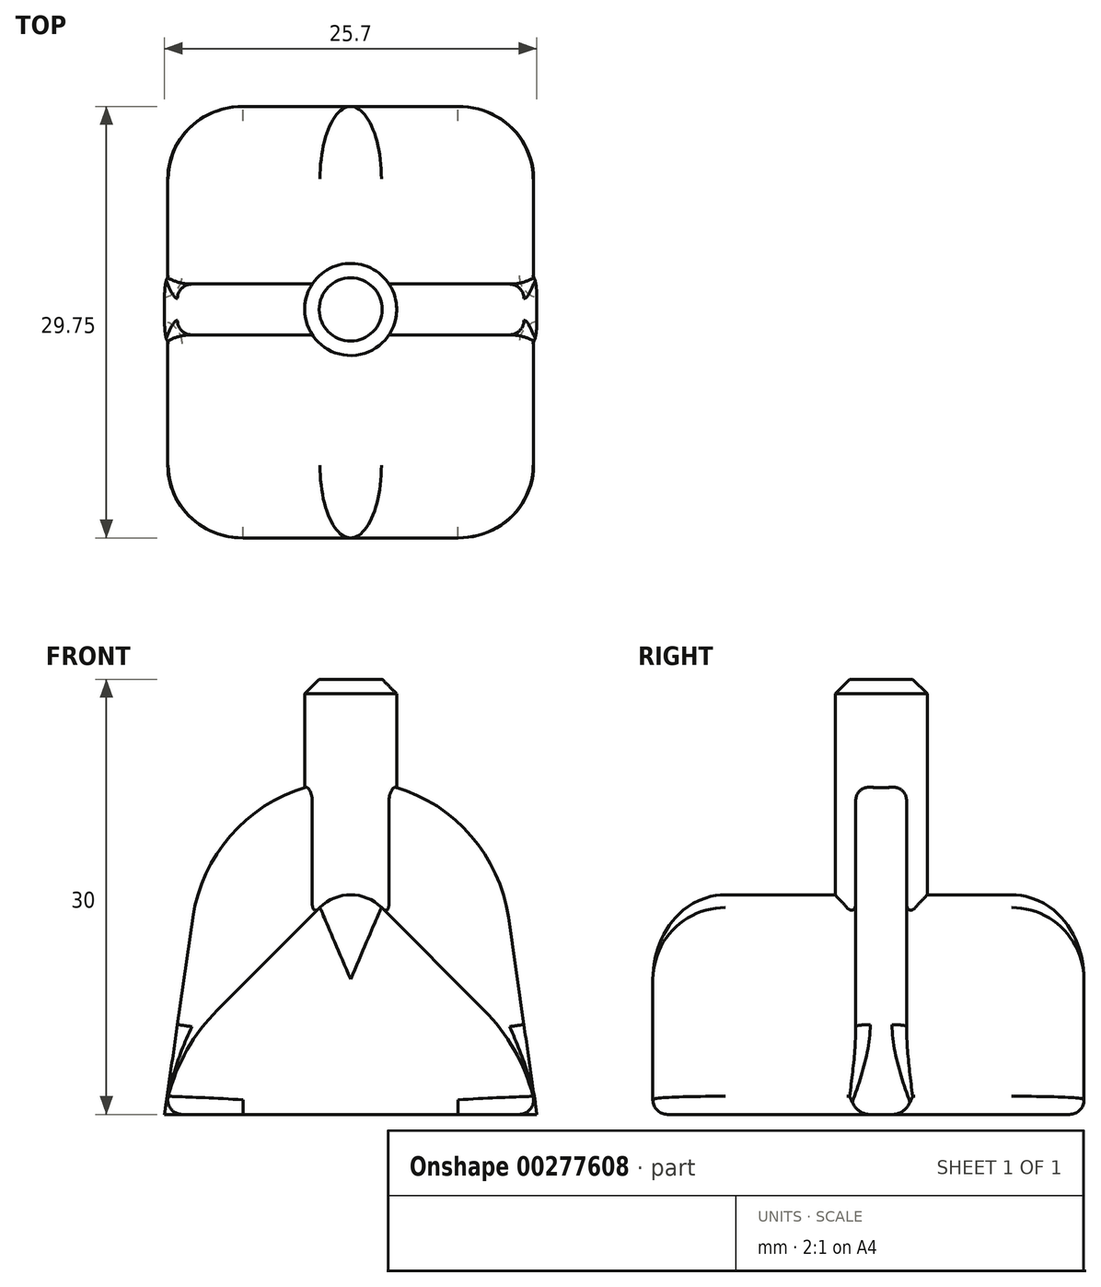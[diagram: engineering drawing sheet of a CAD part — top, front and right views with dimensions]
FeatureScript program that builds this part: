
annotation { "Feature Type Name" : "Feature", "Feature Type Description" : "" }
export const myFeature = defineFeature(function(context is Context, id is Id, definition is map)
    precondition{}
    {
        {
            var Q0;
            Q0=qCreatedBy(makeId("Front.planeOp"),FACE);
            var sketch = newSketch(context, id + "F0", { "sketchPlane" : qUnion([Q0])});
            skArc(sketch, "E0", {"start": v(12.85, 0) * mm, "mid": v(0, 11) * mm, "end": v(-12.85, 0) * mm});
            skLineSegment(sketch, "E1", {"start": v(-9.2, 7.2) * mm, "end": v(-2.12, 14.26) * mm});
            skLineSegment(sketch, "E2", {"start": v(2.12, 14.26) * mm, "end": v(9.2, 7.2) * mm});
            skLineSegment(sketch, "E3", {"start": v(12.85, 0) * mm, "end": v(-12.85, 0) * mm});
            skPoint(sketch, "E4.visualSharp", {"position": v(0, 16.38) * mm});
            skArc(sketch, "E4.filletArc", {"start": v(2.12, 14.26) * mm, "mid": v(0, 15.14) * mm, "end": v(-2.12, 14.26) * mm});
            skCircle(sketch, "E5", {"center": v(0, 12) * mm, "radius": 11 * mm, "construction": true});
            skSolve(sketch);
        }
        {
            var Q0;
            {var subQ0=sQuery(id+"F0.wireOp",EDGE,"E3");Q0=makeQuery(id+"F0.imprint","IMPRINT",FACE,{"disambiguationData":[TD([[makeQuery(id+"F0.imprint","IMPRINT",EDGE,{"derivedFrom":subQ0}),-1.0]])]});}
            var Q1;
            {var subQ0=sQuery(id+"F0.wireOp",EDGE,"E1");Q1=makeQuery(id+"F0.imprint","IMPRINT",FACE,{"disambiguationData":[TD([[makeQuery(id+"F0.imprint","IMPRINT",EDGE,{"derivedFrom":subQ0}),-1.0]])]});}
            extrude(context, id + "F1", {"entities" : qUnion([Q0, Q1]), "endBound" : BoundingType.SYMMETRIC, "depth" : 28 * mm});
        }
        {
            var Q0;
            Q0=qCreatedBy(makeId("Front.planeOp"),FACE);
            var sketch = newSketch(context, id + "F2", { "sketchPlane" : qUnion([Q0])});
            skCircle(sketch, "E6.0", {"center": v(0, 12) * mm, "radius": 11 * mm});
            skArc(sketch, "E7.0", {"start": v(12.85, 0) * mm, "mid": v(0, 11) * mm, "end": v(-12.85, 0) * mm});
            skLineSegment(sketch, "E8", {"start": v(-10.89, 13.57) * mm, "end": v(-12.85, 0) * mm});
            skLineSegment(sketch, "E9", {"start": v(10.89, 13.57) * mm, "end": v(12.85, 0) * mm});
            skLineSegment(sketch, "E10.0", {"start": v(12.85, 0) * mm, "end": v(-12.85, 0) * mm});
            skSolve(sketch);
        }
        {
            var Q0;
            {var subQ0=sQuery(id+"F2.wireOp",EDGE,"E6.0");var subQ1=makeQuery(id+"F2.imprint","INTERSECT",VERTEX,{"derivedFrom":[subQ0,sQuery(id+"F2.wireOp",EDGE,"E8")]});Q0=makeQuery(id+"F2.imprint","IMPRINT",FACE,{"disambiguationData":[TD([[makeQuery(id+"F2.imprint","IMPRINT",EDGE,{"disambiguationData":[TD([[subQ1,1.0]])],"derivedFrom":subQ0}),1.0]])]});}
            var Q1;
            {var subQ0=sQuery(id+"F2.wireOp",EDGE,"E8");Q1=makeQuery(id+"F2.imprint","IMPRINT",FACE,{"disambiguationData":[TD([[makeQuery(id+"F2.imprint","IMPRINT",EDGE,{"derivedFrom":subQ0}),1.0]])]});}
            var Q2;
            Q2=makeQuery(id+"F1.opExtrude","CAP_FACE",FACE,{"disambiguationData":[OSD([sQuery(id+"F0.wireOp",EDGE,"E0"),sQuery(id+"F0.wireOp",EDGE,"E1"),sQuery(id+"F0.wireOp",EDGE,"E2"),sQuery(id+"F0.wireOp",EDGE,"E3"),sQuery(id+"F0.wireOp",EDGE,"E4.filletArc")])],"isStart":false});
            var Q3;
            {var subQ0=sQuery(id+"F2.wireOp",EDGE,"E9");Q3=makeQuery(id+"F2.imprint","IMPRINT",FACE,{"disambiguationData":[TD([[makeQuery(id+"F2.imprint","IMPRINT",EDGE,{"derivedFrom":subQ0}),-1.0]])]});}
            extrude(context, id + "F3", {"entities" : qUnion([Q0, Q1, Q2, Q3]), "operationType" : NewBodyOperationType.ADD, "endBound" : BoundingType.SYMMETRIC, "depth" : 3.5 * mm});
        }
        {
            var Q0;
            {var subQ0=sQuery(id+"F0.wireOp",EDGE,"E0");Q0=makeQuery(id+"F3.opExtrude","CAP_EDGE",EDGE,{"disambiguationData":[OSD([subQ0]),TDD([makeQuery(id+"F1.opExtrude","CAP_EDGE",EDGE,{"disambiguationData":[OSD([subQ0]),TDD([makeQuery(id+"F0.imprint","IMPRINT",EDGE,{"disambiguationData":[TD([[makeQuery(id+"F0.imprint","INTERSECT",VERTEX,{"disambiguationData":[OD(0.0)],"derivedFrom":[subQ0,sQuery(id+"F0.wireOp",EDGE,"E3")]}),-1.0]])],"derivedFrom":subQ0})])],"isStart":false})])],"isStart":false});}
            var Q1;
            {var subQ0=sQuery(id+"F0.wireOp",EDGE,"E0");Q1=makeQuery(id+"F1.opExtrude","CAP_EDGE",EDGE,{"disambiguationData":[OSD([subQ0]),TDD([makeQuery(id+"F0.imprint","IMPRINT",EDGE,{"disambiguationData":[TD([[makeQuery(id+"F0.imprint","INTERSECT",VERTEX,{"disambiguationData":[OD(0.0)],"derivedFrom":[subQ0,sQuery(id+"F0.wireOp",EDGE,"E3")]}),-1.0]])],"derivedFrom":subQ0})])],"isStart":true});}
            fillet(context, id + "F4", {"entities" : qUnion([Q0, Q1]), "radius" : 5 * mm, "tangentPropagation" : true, "allowEdgeOverflow" : false});
        }
        {
            var Q0;
            {var subQ0=sQuery(id+"F0.wireOp",EDGE,"E0");var subQ1=makeQuery(id+"F0.imprint","IMPRINT",EDGE,{"disambiguationData":[TD([[makeQuery(id+"F0.imprint","INTERSECT",VERTEX,{"disambiguationData":[OD(1.0)],"derivedFrom":[subQ0,sQuery(id+"F0.wireOp",EDGE,"E3")]}),1.0]])],"derivedFrom":subQ0});var subQ2=sQuery(id+"F2.wireOp",EDGE,"E7.0");Q0=makeQuery(id+"F3.boolean.opBoolean","SPLIT",EDGE,{"disambiguationData":[topologyDisambiguationEdgeConnected([makeQuery(id+"F3.opExtrude","SWEPT_FACE",FACE,{"disambiguationData":[OSD([subQ0]),TDD([makeQuery(id+"F1.opExtrude","CAP_EDGE",EDGE,{"disambiguationData":[OSD([subQ0]),TDD([subQ1])],"isStart":false})])]})])],"derivedFrom":makeQuery(id+"F3.opExtrude","CAP_EDGE",EDGE,{"disambiguationData":[OSD([subQ2])],"isStart":false})});}
            var Q1;
            {var subQ0=sQuery(id+"F0.wireOp",EDGE,"E0");var subQ1=makeQuery(id+"F0.imprint","IMPRINT",EDGE,{"disambiguationData":[TD([[makeQuery(id+"F0.imprint","INTERSECT",VERTEX,{"disambiguationData":[OD(1.0)],"derivedFrom":[subQ0,sQuery(id+"F0.wireOp",EDGE,"E3")]}),1.0]])],"derivedFrom":subQ0});var subQ2=sQuery(id+"F2.wireOp",EDGE,"E7.0");Q1=makeQuery(id+"F3.boolean.opBoolean","SPLIT",EDGE,{"disambiguationData":[topologyDisambiguationEdgeConnected([makeQuery(id+"F3.opExtrude","SWEPT_FACE",FACE,{"disambiguationData":[OSD([subQ0]),TDD([makeQuery(id+"F1.opExtrude","CAP_EDGE",EDGE,{"disambiguationData":[OSD([subQ0]),TDD([subQ1])],"isStart":false})])]})])],"derivedFrom":makeQuery(id+"F3.opExtrude","CAP_EDGE",EDGE,{"disambiguationData":[OSD([subQ2])],"isStart":true})});}
            fillet(context, id + "F5", {"entities" : qUnion([Q0, Q1]), "radius" : .6 * mm, "tangentPropagation" : true, "allowEdgeOverflow" : false});
        }
        {
            var Q0;
            Q0=makeQuery(id+"F3.opExtrude","CAP_EDGE",EDGE,{"disambiguationData":[OSD([sQuery(id+"F2.wireOp",EDGE,"E8")])],"isStart":true});
            var Q1;
            Q1=makeQuery(id+"F3.opExtrude","CAP_EDGE",EDGE,{"disambiguationData":[OSD([sQuery(id+"F2.wireOp",EDGE,"E8")])],"isStart":false});
            fillet(context, id + "F6", {"entities" : qUnion([Q0, Q1]), "radius" : 1 * mm, "tangentPropagation" : true, "allowEdgeOverflow" : false});
        }
        {
            var Q0;
            Q0=qCreatedBy(makeId("Top.planeOp"),FACE);
            var sketch = newSketch(context, id + "F7", { "sketchPlane" : qUnion([Q0])});
            skCircle(sketch, "E11", {"center": v(0, 0) * mm, "radius": 3.18 * mm});
            skSolve(sketch);
        }
        {
            var Q0;
            Q0 = qSketchRegion(id + "F7", true);
            extrude(context, id + "F8", {"entities" : qUnion([Q0]), "operationType" : NewBodyOperationType.ADD, "depth" : 30 * mm});
        }
        {
            var Q0;
            Q0=makeQuery(id+"F8.opExtrude","CAP_EDGE",EDGE,{"disambiguationData":[OSD([sQuery(id+"F7.wireOp",EDGE,"E11")])],"isStart":false});
            chamfer(context, id + "F9", {"entities" : qUnion([Q0]), "width" : 1 * mm, "tangentPropagation" : true});
        }
    });
